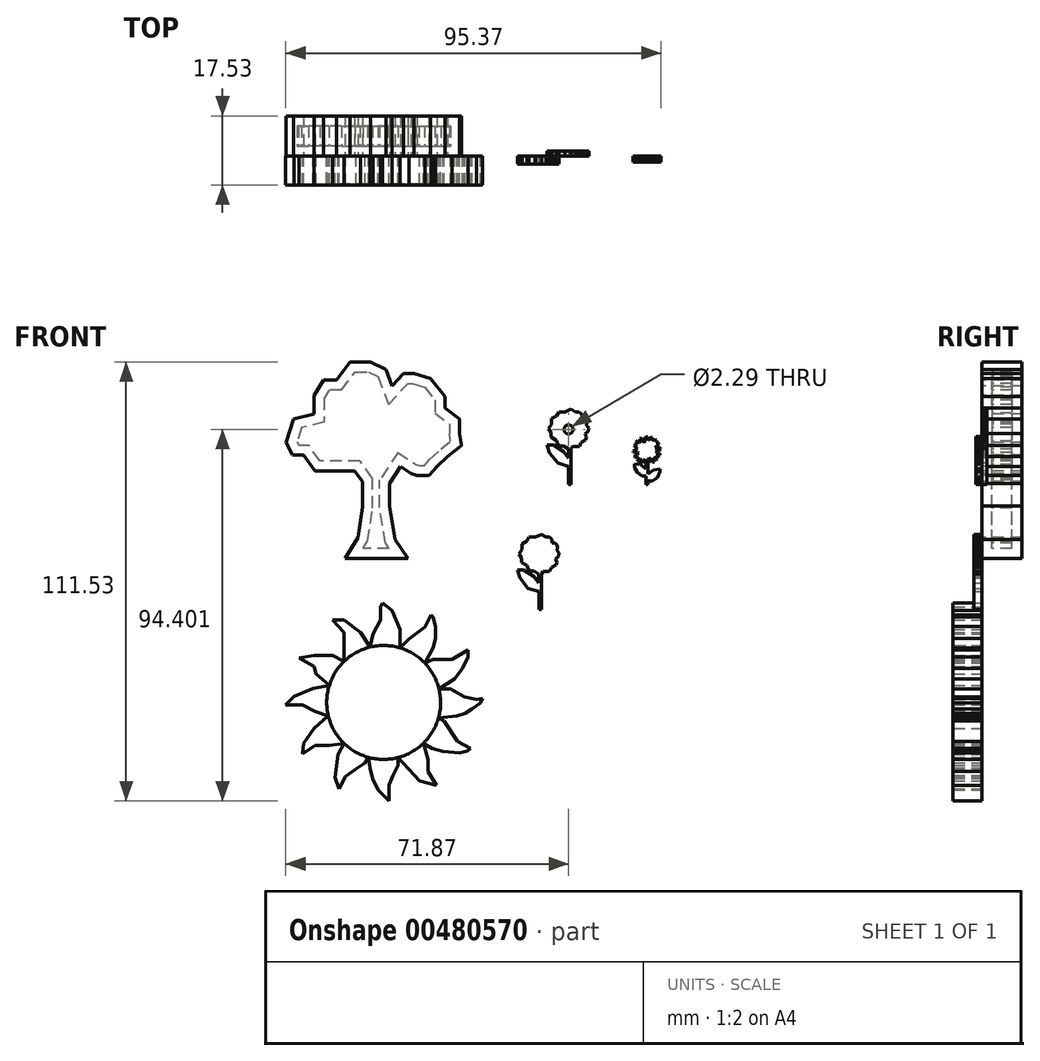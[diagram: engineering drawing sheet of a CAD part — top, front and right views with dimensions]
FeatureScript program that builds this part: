
annotation { "Feature Type Name" : "Feature", "Feature Type Description" : "" }
export const myFeature = defineFeature(function(context is Context, id is Id, definition is map)
    precondition{}
    {
        {
            var Q0;
            Q0=qCreatedBy(makeId("Front.planeOp"),FACE);
            var sketch = newSketch(context, id + "F0", { "sketchPlane" : qUnion([Q0])});
            skLineSegment(sketch, "E0", {"start": v(-33.39, 1.15) * mm, "end": v(-36.7, 6.04) * mm});
            skLineSegment(sketch, "E1", {"start": v(-36.7, 6.04) * mm, "end": v(-38.13, 14.53) * mm});
            skLineSegment(sketch, "E2", {"start": v(-38.13, 14.53) * mm, "end": v(-38.13, 20.3) * mm});
            skLineSegment(sketch, "E3", {"start": v(-49.36, 1.15) * mm, "end": v(-46.05, 6.48) * mm});
            skLineSegment(sketch, "E4", {"start": v(-46.05, 6.48) * mm, "end": v(-44.9, 14.25) * mm});
            skLineSegment(sketch, "E5", {"start": v(-44.9, 14.25) * mm, "end": v(-44.9, 20.72) * mm});
            skLineSegment(sketch, "E6", {"start": v(-44.9, 20.72) * mm, "end": v(-46.91, 23.46) * mm});
            skLineSegment(sketch, "E7", {"start": v(-28.06, 22.24) * mm, "end": v(-26.05, 24.6) * mm});
            skLineSegment(sketch, "E8", {"start": v(-46.91, 23.46) * mm, "end": v(-49.8, 23.46) * mm});
            skLineSegment(sketch, "E9", {"start": v(-49.8, 23.46) * mm, "end": v(-52.81, 23.46) * mm});
            skLineSegment(sketch, "E10", {"start": v(-52.81, 23.46) * mm, "end": v(-56.99, 23.46) * mm});
            skLineSegment(sketch, "E11", {"start": v(-56.99, 23.46) * mm, "end": v(-58.52, 25.54) * mm});
            skLineSegment(sketch, "E12", {"start": v(-58.52, 25.54) * mm, "end": v(-59.94, 27.46) * mm});
            skLineSegment(sketch, "E13", {"start": v(-51.52, 46.48) * mm, "end": v(-54.83, 46.48) * mm});
            skLineSegment(sketch, "E14", {"start": v(-54.83, 46.48) * mm, "end": v(-57.27, 42.6) * mm});
            skLineSegment(sketch, "E15", {"start": v(-57.27, 42.6) * mm, "end": v(-57.27, 37.85) * mm});
            skLineSegment(sketch, "E16", {"start": v(-57.27, 37.85) * mm, "end": v(-62.45, 36.55) * mm});
            skLineSegment(sketch, "E17", {"start": v(-62.45, 36.55) * mm, "end": v(-64.32, 30.65) * mm});
            skLineSegment(sketch, "E18", {"start": v(-64.32, 30.65) * mm, "end": v(-62.74, 27.46) * mm});
            skLineSegment(sketch, "E19", {"start": v(-62.74, 27.46) * mm, "end": v(-59.94, 27.46) * mm});
            skLineSegment(sketch, "E20", {"start": v(-51.52, 46.48) * mm, "end": v(-48.06, 51.09) * mm});
            skLineSegment(sketch, "E21", {"start": v(-48.06, 51.09) * mm, "end": v(-42.88, 51.09) * mm});
            skLineSegment(sketch, "E22", {"start": v(-42.88, 51.09) * mm, "end": v(-39, 49.21) * mm});
            skLineSegment(sketch, "E23", {"start": v(-39, 49.21) * mm, "end": v(-37.41, 45.04) * mm});
            skLineSegment(sketch, "E24", {"start": v(-37.41, 45.04) * mm, "end": v(-34.54, 48.2) * mm});
            skLineSegment(sketch, "E25", {"start": v(-34.54, 48.2) * mm, "end": v(-31.8, 48.2) * mm});
            skLineSegment(sketch, "E26", {"start": v(-31.8, 48.2) * mm, "end": v(-27.63, 46.91) * mm});
            skLineSegment(sketch, "E27", {"start": v(-27.63, 46.91) * mm, "end": v(-24.03, 42.3) * mm});
            skLineSegment(sketch, "E28", {"start": v(-24.03, 42.3) * mm, "end": v(-24.03, 39.43) * mm});
            skLineSegment(sketch, "E29", {"start": v(-24.03, 39.43) * mm, "end": v(-20.3, 36.55) * mm});
            skLineSegment(sketch, "E30", {"start": v(-20.3, 36.55) * mm, "end": v(-20.3, 32.95) * mm});
            skLineSegment(sketch, "E31", {"start": v(-26.05, 24.6) * mm, "end": v(-23.31, 27.05) * mm});
            skLineSegment(sketch, "E32", {"start": v(-23.31, 27.05) * mm, "end": v(-19.86, 29.93) * mm});
            skLineSegment(sketch, "E33", {"start": v(-19.86, 29.93) * mm, "end": v(-20.3, 32.95) * mm});
            skLineSegment(sketch, "E34", {"start": v(-35.26, 24.6) * mm, "end": v(-38.13, 20.3) * mm});
            skLineSegment(sketch, "E35", {"start": v(-35.26, 24.6) * mm, "end": v(-32.57, 22.81) * mm});
            skLineSegment(sketch, "E36", {"start": v(-32.57, 22.81) * mm, "end": v(-31.1, 22.24) * mm});
            skLineSegment(sketch, "E37", {"start": v(-31.1, 22.24) * mm, "end": v(-28.06, 22.24) * mm});
            skLineSegment(sketch, "E38", {"start": v(-33.39, 1.15) * mm, "end": v(-49.36, 1.15) * mm});
            skSolve(sketch);
        }
        {
            var Q0;
            Q0=makeQuery(id+"F0.imprint","IMPRINT",FACE,{"disambiguationData":[TD([[makeQuery(id+"F0.imprint","IMPRINT",EDGE,{"derivedFrom":sQuery(id+"F0.wireOp",EDGE,"E0")}),1.0]])]});
            extrude(context, id + "F1", {"entities" : qUnion([Q0]), "oppositeDirection" : true, "depth" : 10.16 * mm});
        }
        {
            var Q0;
            Q0=makeQuery(id+"F1.opExtrude","CAP_FACE",FACE,{"disambiguationData":[OSD([sQuery(id+"F0.wireOp",EDGE,"E0"),sQuery(id+"F0.wireOp",EDGE,"E1"),sQuery(id+"F0.wireOp",EDGE,"E2"),sQuery(id+"F0.wireOp",EDGE,"E3"),sQuery(id+"F0.wireOp",EDGE,"E4"),sQuery(id+"F0.wireOp",EDGE,"E5"),sQuery(id+"F0.wireOp",EDGE,"E6"),sQuery(id+"F0.wireOp",EDGE,"E7"),sQuery(id+"F0.wireOp",EDGE,"E8"),sQuery(id+"F0.wireOp",EDGE,"E9"),sQuery(id+"F0.wireOp",EDGE,"E10"),sQuery(id+"F0.wireOp",EDGE,"E11"),sQuery(id+"F0.wireOp",EDGE,"E12"),sQuery(id+"F0.wireOp",EDGE,"E13"),sQuery(id+"F0.wireOp",EDGE,"E14"),sQuery(id+"F0.wireOp",EDGE,"E15"),sQuery(id+"F0.wireOp",EDGE,"E16"),sQuery(id+"F0.wireOp",EDGE,"E17"),sQuery(id+"F0.wireOp",EDGE,"E18"),sQuery(id+"F0.wireOp",EDGE,"E19"),sQuery(id+"F0.wireOp",EDGE,"E20"),sQuery(id+"F0.wireOp",EDGE,"E21"),sQuery(id+"F0.wireOp",EDGE,"E22"),sQuery(id+"F0.wireOp",EDGE,"E23"),sQuery(id+"F0.wireOp",EDGE,"E24"),sQuery(id+"F0.wireOp",EDGE,"E25"),sQuery(id+"F0.wireOp",EDGE,"E26"),sQuery(id+"F0.wireOp",EDGE,"E27"),sQuery(id+"F0.wireOp",EDGE,"E28"),sQuery(id+"F0.wireOp",EDGE,"E29"),sQuery(id+"F0.wireOp",EDGE,"E30"),sQuery(id+"F0.wireOp",EDGE,"E31"),sQuery(id+"F0.wireOp",EDGE,"E32"),sQuery(id+"F0.wireOp",EDGE,"E33"),sQuery(id+"F0.wireOp",EDGE,"E34"),sQuery(id+"F0.wireOp",EDGE,"E35"),sQuery(id+"F0.wireOp",EDGE,"E36"),sQuery(id+"F0.wireOp",EDGE,"E37"),sQuery(id+"F0.wireOp",EDGE,"E38")])],"isStart":true});
            var Q1;
            Q1=makeQuery(id+"F1.opExtrude","SWEPT_BODY",BODY,{"disambiguationData":[OSD([sQuery(id+"F0.wireOp",EDGE,"E0"),sQuery(id+"F0.wireOp",EDGE,"E1"),sQuery(id+"F0.wireOp",EDGE,"E2"),sQuery(id+"F0.wireOp",EDGE,"E3"),sQuery(id+"F0.wireOp",EDGE,"E4"),sQuery(id+"F0.wireOp",EDGE,"E5"),sQuery(id+"F0.wireOp",EDGE,"E6"),sQuery(id+"F0.wireOp",EDGE,"E7"),sQuery(id+"F0.wireOp",EDGE,"E8"),sQuery(id+"F0.wireOp",EDGE,"E9"),sQuery(id+"F0.wireOp",EDGE,"E10"),sQuery(id+"F0.wireOp",EDGE,"E11"),sQuery(id+"F0.wireOp",EDGE,"E12"),sQuery(id+"F0.wireOp",EDGE,"E13"),sQuery(id+"F0.wireOp",EDGE,"E14"),sQuery(id+"F0.wireOp",EDGE,"E15"),sQuery(id+"F0.wireOp",EDGE,"E16"),sQuery(id+"F0.wireOp",EDGE,"E17"),sQuery(id+"F0.wireOp",EDGE,"E18"),sQuery(id+"F0.wireOp",EDGE,"E19"),sQuery(id+"F0.wireOp",EDGE,"E20"),sQuery(id+"F0.wireOp",EDGE,"E21"),sQuery(id+"F0.wireOp",EDGE,"E22"),sQuery(id+"F0.wireOp",EDGE,"E23"),sQuery(id+"F0.wireOp",EDGE,"E24"),sQuery(id+"F0.wireOp",EDGE,"E25"),sQuery(id+"F0.wireOp",EDGE,"E26"),sQuery(id+"F0.wireOp",EDGE,"E27"),sQuery(id+"F0.wireOp",EDGE,"E28"),sQuery(id+"F0.wireOp",EDGE,"E29"),sQuery(id+"F0.wireOp",EDGE,"E30"),sQuery(id+"F0.wireOp",EDGE,"E31"),sQuery(id+"F0.wireOp",EDGE,"E32"),sQuery(id+"F0.wireOp",EDGE,"E33"),sQuery(id+"F0.wireOp",EDGE,"E34"),sQuery(id+"F0.wireOp",EDGE,"E35"),sQuery(id+"F0.wireOp",EDGE,"E36"),sQuery(id+"F0.wireOp",EDGE,"E37"),sQuery(id+"F0.wireOp",EDGE,"E38")])]});
            shell(context, id + "F2", {"isHollow" : true, "entities" : qUnion([Q0]), "parts" : qUnion([Q1]), "thickness" : 2.54 * mm});
        }
        {
            var Q0;
            Q0=qCreatedBy(makeId("Front.planeOp"),FACE);
            var sketch = newSketch(context, id + "F3", { "sketchPlane" : qUnion([Q0])});
            skLineSegment(sketch, "E39", {"start": v(7.99, 20) * mm, "end": v(7.99, 29.07) * mm});
            skLineSegment(sketch, "E40", {"start": v(7.44, 20) * mm, "end": v(7.44, 24.53) * mm});
            skPoint(sketch, "E40.endSnap0", {"position": v(7.99, 24.53) * mm});
            skLineSegment(sketch, "E41", {"start": v(7.44, 24.53) * mm, "end": v(4.66, 25.38) * mm});
            skLineSegment(sketch, "E42", {"start": v(4.66, 25.38) * mm, "end": v(2.54, 27.98) * mm});
            skLineSegment(sketch, "E43", {"start": v(2.54, 27.98) * mm, "end": v(1.87, 30.04) * mm});
            skLineSegment(sketch, "E44", {"start": v(1.87, 30.04) * mm, "end": v(3.5, 30.04) * mm});
            skLineSegment(sketch, "E45", {"start": v(3.5, 30.04) * mm, "end": v(6.17, 28.4) * mm});
            skLineSegment(sketch, "E46", {"start": v(6.17, 28.4) * mm, "end": v(7.32, 26.77) * mm});
            skLineSegment(sketch, "E47", {"start": v(7.32, 26.77) * mm, "end": v(7.32, 29) * mm});
            skLineSegment(sketch, "E48", {"start": v(7.32, 29) * mm, "end": v(6.1, 29.73) * mm});
            skLineSegment(sketch, "E49", {"start": v(6.1, 29.73) * mm, "end": v(4.84, 29.73) * mm});
            skPoint(sketch, "E49.endSnap0", {"position": v(4.84, 29.22) * mm});
            skLineSegment(sketch, "E50", {"start": v(4.84, 29.73) * mm, "end": v(4.3, 31.13) * mm});
            skLineSegment(sketch, "E51", {"start": v(4.3, 31.13) * mm, "end": v(2.89, 31.99) * mm});
            skLineSegment(sketch, "E52", {"start": v(2.89, 31.99) * mm, "end": v(2.89, 33.12) * mm});
            skLineSegment(sketch, "E53", {"start": v(2.89, 33.12) * mm, "end": v(2.36, 34.15) * mm});
            skLineSegment(sketch, "E54", {"start": v(2.36, 34.15) * mm, "end": v(3.04, 35.27) * mm});
            skLineSegment(sketch, "E55", {"start": v(3.04, 35.27) * mm, "end": v(3.04, 36.7) * mm});
            skLineSegment(sketch, "E56", {"start": v(3.04, 36.7) * mm, "end": v(4.3, 37.36) * mm});
            skLineSegment(sketch, "E57", {"start": v(4.3, 37.36) * mm, "end": v(4.91, 38.37) * mm});
            skLineSegment(sketch, "E58", {"start": v(4.91, 38.37) * mm, "end": v(6.53, 38.37) * mm});
            skLineSegment(sketch, "E59", {"start": v(6.53, 38.37) * mm, "end": v(7.99, 39.11) * mm});
            skLineSegment(sketch, "E60", {"start": v(7.99, 39.11) * mm, "end": v(9.2, 38.37) * mm});
            skLineSegment(sketch, "E61", {"start": v(7.99, 29.07) * mm, "end": v(8.42, 29.67) * mm});
            skLineSegment(sketch, "E62", {"start": v(8.42, 29.67) * mm, "end": v(10.12, 29.67) * mm});
            skLineSegment(sketch, "E63", {"start": v(10.12, 29.67) * mm, "end": v(10.52, 30.7) * mm});
            skLineSegment(sketch, "E64", {"start": v(10.52, 30.7) * mm, "end": v(11.7, 31.3) * mm});
            skLineSegment(sketch, "E65", {"start": v(11.7, 31.3) * mm, "end": v(11.95, 32) * mm});
            skLineSegment(sketch, "E66", {"start": v(11.95, 32) * mm, "end": v(11.59, 32.81) * mm});
            skLineSegment(sketch, "E67", {"start": v(11.59, 32.81) * mm, "end": v(12.36, 33.43) * mm});
            skLineSegment(sketch, "E68", {"start": v(12.36, 33.43) * mm, "end": v(12.53, 34.35) * mm});
            skLineSegment(sketch, "E69", {"start": v(12.53, 34.35) * mm, "end": v(11.95, 34.95) * mm});
            skLineSegment(sketch, "E70", {"start": v(11.95, 34.95) * mm, "end": v(12.1, 35.77) * mm});
            skLineSegment(sketch, "E71", {"start": v(12.1, 35.77) * mm, "end": v(11.95, 36.38) * mm});
            skLineSegment(sketch, "E72", {"start": v(11.95, 36.38) * mm, "end": v(11.5, 36.84) * mm});
            skLineSegment(sketch, "E73", {"start": v(11.5, 36.84) * mm, "end": v(10.76, 36.84) * mm});
            skLineSegment(sketch, "E74", {"start": v(10.76, 36.84) * mm, "end": v(10.76, 37.73) * mm});
            skLineSegment(sketch, "E75", {"start": v(10.76, 37.73) * mm, "end": v(10.1, 38.4) * mm});
            skLineSegment(sketch, "E76", {"start": v(10.1, 38.4) * mm, "end": v(9.2, 38.37) * mm});
            skLineSegment(sketch, "E77", {"start": v(7.99, 20) * mm, "end": v(7.44, 20) * mm});
            skLineSegment(sketch, "E78", {"start": v(7.32, 26.77) * mm, "end": v(7.44, 24.53) * mm});
            skSolve(sketch);
        }
        {
            var Q0;
            Q0=makeQuery(id+"F3.imprint","IMPRINT",FACE,{"disambiguationData":[TD([[makeQuery(id+"F3.imprint","IMPRINT",EDGE,{"derivedFrom":sQuery(id+"F3.wireOp",EDGE,"E39")}),1.0]])]});
            var Q1;
            Q1=makeQuery(id+"F3.imprint","IMPRINT",FACE,{"disambiguationData":[TD([[makeQuery(id+"F3.imprint","IMPRINT",EDGE,{"derivedFrom":sQuery(id+"F3.wireOp",EDGE,"E41")}),-1.0]])]});
            extrude(context, id + "F4", {"entities" : qUnion([Q0, Q1]), "oppositeDirection" : true, "depth" : 1.27 * mm});
        }
        {
            var Q0;
            Q0=qCreatedBy(makeId("Front.planeOp"),FACE);
            var sketch = newSketch(context, id + "F5", { "sketchPlane" : qUnion([Q0])});
            skCircle(sketch, "E79", {"center": v(7.4, 33.96) * mm, "radius": 1.58 * mm});
            skSolve(sketch);
        }
        {
            var Q0;
            Q0=sQuery(id+"F5.wireOp",VERTEX,"E79.center");
            var Q1;
            Q1=makeQuery(id+"F4.opExtrude","SWEPT_BODY",BODY,{"disambiguationData":[OSD([sQuery(id+"F3.wireOp",EDGE,"E39"),sQuery(id+"F3.wireOp",EDGE,"E40"),sQuery(id+"F3.wireOp",EDGE,"E41"),sQuery(id+"F3.wireOp",EDGE,"E42"),sQuery(id+"F3.wireOp",EDGE,"E43"),sQuery(id+"F3.wireOp",EDGE,"E44"),sQuery(id+"F3.wireOp",EDGE,"E45"),sQuery(id+"F3.wireOp",EDGE,"E46"),sQuery(id+"F3.wireOp",EDGE,"E47"),sQuery(id+"F3.wireOp",EDGE,"E48"),sQuery(id+"F3.wireOp",EDGE,"E49"),sQuery(id+"F3.wireOp",EDGE,"E50"),sQuery(id+"F3.wireOp",EDGE,"E51"),sQuery(id+"F3.wireOp",EDGE,"E52"),sQuery(id+"F3.wireOp",EDGE,"E53"),sQuery(id+"F3.wireOp",EDGE,"E54"),sQuery(id+"F3.wireOp",EDGE,"E55"),sQuery(id+"F3.wireOp",EDGE,"E56"),sQuery(id+"F3.wireOp",EDGE,"E57"),sQuery(id+"F3.wireOp",EDGE,"E58"),sQuery(id+"F3.wireOp",EDGE,"E59"),sQuery(id+"F3.wireOp",EDGE,"E60"),sQuery(id+"F3.wireOp",EDGE,"E61"),sQuery(id+"F3.wireOp",EDGE,"E62"),sQuery(id+"F3.wireOp",EDGE,"E63"),sQuery(id+"F3.wireOp",EDGE,"E64"),sQuery(id+"F3.wireOp",EDGE,"E65"),sQuery(id+"F3.wireOp",EDGE,"E66"),sQuery(id+"F3.wireOp",EDGE,"E67"),sQuery(id+"F3.wireOp",EDGE,"E68"),sQuery(id+"F3.wireOp",EDGE,"E69"),sQuery(id+"F3.wireOp",EDGE,"E70"),sQuery(id+"F3.wireOp",EDGE,"E71"),sQuery(id+"F3.wireOp",EDGE,"E72"),sQuery(id+"F3.wireOp",EDGE,"E73"),sQuery(id+"F3.wireOp",EDGE,"E74"),sQuery(id+"F3.wireOp",EDGE,"E75"),sQuery(id+"F3.wireOp",EDGE,"E76"),sQuery(id+"F3.wireOp",EDGE,"E77")])]});
            hole(context, id + "F6", {"style" : HoleStyle.C_BORE, "endStyle" : HoleEndStyle.THROUGH, "holeDiameter" : 1.14 * mm, "cBoreDiameter" : 2.3 * mm, "cBoreDepth" : 12.7 * mm, "tappedDepth" : 12.7 * mm, "tapClearance" : 3, "locations" : qUnion([Q0]), "scope" : qUnion([Q1])});
        }
        {
            var Q0;
            Q0=qCreatedBy(makeId("Front.planeOp"),FACE);
            var sketch = newSketch(context, id + "F7", { "sketchPlane" : qUnion([Q0])});
            skLineSegment(sketch, "E80", {"start": v(0.48, -11.79) * mm, "end": v(0.48, -2.71) * mm});
            skLineSegment(sketch, "E81", {"start": v(-0.06, -11.79) * mm, "end": v(-0.06, -7.25) * mm});
            skPoint(sketch, "E81.endSnap0", {"position": v(0.48, -7.25) * mm});
            skLineSegment(sketch, "E82", {"start": v(-0.06, -7.25) * mm, "end": v(-2.85, -6.4) * mm});
            skLineSegment(sketch, "E83", {"start": v(-2.85, -6.4) * mm, "end": v(-4.96, -3.8) * mm});
            skLineSegment(sketch, "E84", {"start": v(-4.96, -3.8) * mm, "end": v(-5.63, -1.74) * mm});
            skLineSegment(sketch, "E85", {"start": v(-5.63, -1.74) * mm, "end": v(-4, -1.74) * mm});
            skLineSegment(sketch, "E86", {"start": v(-4, -1.74) * mm, "end": v(-1.33, -3.38) * mm});
            skLineSegment(sketch, "E87", {"start": v(-1.33, -3.38) * mm, "end": v(-0.18, -5.01) * mm});
            skLineSegment(sketch, "E88", {"start": v(-0.18, -5.01) * mm, "end": v(-0.18, -2.77) * mm});
            skLineSegment(sketch, "E89", {"start": v(-0.18, -2.77) * mm, "end": v(-1.4, -2.05) * mm});
            skLineSegment(sketch, "E90", {"start": v(-1.4, -2.05) * mm, "end": v(-2.66, -2.05) * mm});
            skPoint(sketch, "E90.endSnap0", {"position": v(-2.66, -2.56) * mm});
            skLineSegment(sketch, "E91", {"start": v(-2.66, -2.05) * mm, "end": v(-3.2, -0.66) * mm});
            skLineSegment(sketch, "E92", {"start": v(-3.2, -0.66) * mm, "end": v(-4.61, 0.2) * mm});
            skLineSegment(sketch, "E93", {"start": v(-4.61, 0.2) * mm, "end": v(-4.61, 1.34) * mm});
            skLineSegment(sketch, "E94", {"start": v(-4.61, 1.34) * mm, "end": v(-5.15, 2.37) * mm});
            skLineSegment(sketch, "E95", {"start": v(-5.15, 2.37) * mm, "end": v(-4.46, 3.49) * mm});
            skLineSegment(sketch, "E96", {"start": v(-4.46, 3.49) * mm, "end": v(-4.46, 4.91) * mm});
            skLineSegment(sketch, "E97", {"start": v(-4.46, 4.91) * mm, "end": v(-3.2, 5.58) * mm});
            skLineSegment(sketch, "E98", {"start": v(-3.2, 5.58) * mm, "end": v(-2.59, 6.59) * mm});
            skLineSegment(sketch, "E99", {"start": v(-2.59, 6.59) * mm, "end": v(-0.97, 6.59) * mm});
            skLineSegment(sketch, "E100", {"start": v(-0.97, 6.59) * mm, "end": v(0.48, 7.33) * mm});
            skLineSegment(sketch, "E101", {"start": v(0.48, 7.33) * mm, "end": v(1.7, 6.59) * mm});
            skLineSegment(sketch, "E102", {"start": v(0.48, -2.71) * mm, "end": v(0.92, -2.11) * mm});
            skLineSegment(sketch, "E103", {"start": v(0.92, -2.11) * mm, "end": v(2.62, -2.11) * mm});
            skLineSegment(sketch, "E104", {"start": v(2.62, -2.11) * mm, "end": v(3.01, -1.09) * mm});
            skLineSegment(sketch, "E105", {"start": v(3.01, -1.09) * mm, "end": v(4.2, -0.49) * mm});
            skLineSegment(sketch, "E106", {"start": v(4.2, -0.49) * mm, "end": v(4.45, 0.22) * mm});
            skLineSegment(sketch, "E107", {"start": v(4.45, 0.22) * mm, "end": v(4.08, 1.03) * mm});
            skLineSegment(sketch, "E108", {"start": v(4.08, 1.03) * mm, "end": v(4.85, 1.65) * mm});
            skLineSegment(sketch, "E109", {"start": v(4.85, 1.65) * mm, "end": v(5.02, 2.57) * mm});
            skLineSegment(sketch, "E110", {"start": v(5.02, 2.57) * mm, "end": v(4.45, 3.17) * mm});
            skLineSegment(sketch, "E111", {"start": v(4.45, 3.17) * mm, "end": v(4.6, 4) * mm});
            skLineSegment(sketch, "E112", {"start": v(4.6, 4) * mm, "end": v(4.45, 4.6) * mm});
            skLineSegment(sketch, "E113", {"start": v(4.45, 4.6) * mm, "end": v(4, 5.06) * mm});
            skLineSegment(sketch, "E114", {"start": v(4, 5.06) * mm, "end": v(3.25, 5.06) * mm});
            skLineSegment(sketch, "E115", {"start": v(3.25, 5.06) * mm, "end": v(3.25, 5.95) * mm});
            skLineSegment(sketch, "E116", {"start": v(3.25, 5.95) * mm, "end": v(2.6, 6.62) * mm});
            skLineSegment(sketch, "E117", {"start": v(2.6, 6.62) * mm, "end": v(1.7, 6.59) * mm});
            skLineSegment(sketch, "E118", {"start": v(0.48, -11.79) * mm, "end": v(-0.06, -11.79) * mm});
            skLineSegment(sketch, "E119", {"start": v(-0.18, -5.01) * mm, "end": v(-0.06, -7.25) * mm});
            skSolve(sketch);
        }
        {
            var Q0;
            Q0=makeQuery(id+"F7.imprint","IMPRINT",FACE,{"disambiguationData":[TD([[makeQuery(id+"F7.imprint","IMPRINT",EDGE,{"derivedFrom":sQuery(id+"F7.wireOp",EDGE,"E80")}),1.0]])]});
            var Q1;
            Q1=makeQuery(id+"F7.imprint","IMPRINT",FACE,{"disambiguationData":[TD([[makeQuery(id+"F7.imprint","IMPRINT",EDGE,{"derivedFrom":sQuery(id+"F7.wireOp",EDGE,"E82")}),-1.0]])]});
            extrude(context, id + "F8", {"entities" : qUnion([Q0, Q1]), "depth" : 2.03 * mm});
        }
        {
            var Q0;
            Q0=qCreatedBy(makeId("Front.planeOp"),FACE);
            var sketch = newSketch(context, id + "F9", { "sketchPlane" : qUnion([Q0])});
            skLineSegment(sketch, "E120", {"start": v(27.09, 20.02) * mm, "end": v(27.09, 22.14) * mm});
            skLineSegment(sketch, "E121", {"start": v(27.09, 22.14) * mm, "end": v(26.1, 22.14) * mm});
            skLineSegment(sketch, "E122", {"start": v(26.1, 22.14) * mm, "end": v(24.9, 23.02) * mm});
            skLineSegment(sketch, "E123", {"start": v(24.9, 23.02) * mm, "end": v(24.14, 24.3) * mm});
            skLineSegment(sketch, "E124", {"start": v(24.14, 24.3) * mm, "end": v(24.14, 25.24) * mm});
            skLineSegment(sketch, "E125", {"start": v(24.14, 25.24) * mm, "end": v(25.27, 25.06) * mm});
            skLineSegment(sketch, "E126", {"start": v(25.27, 25.06) * mm, "end": v(25.27, 25.89) * mm});
            skLineSegment(sketch, "E127", {"start": v(28.72, 20.83) * mm, "end": v(29.97, 21.8) * mm});
            skLineSegment(sketch, "E128", {"start": v(29.97, 21.8) * mm, "end": v(30.6, 23.25) * mm});
            skLineSegment(sketch, "E129", {"start": v(30.6, 23.25) * mm, "end": v(30.6, 23.93) * mm});
            skLineSegment(sketch, "E130", {"start": v(30.6, 23.93) * mm, "end": v(29, 23.65) * mm});
            skLineSegment(sketch, "E131", {"start": v(29, 23.65) * mm, "end": v(28.04, 23) * mm});
            skLineSegment(sketch, "E132", {"start": v(27.55, 25.12) * mm, "end": v(27.13, 25.7) * mm});
            skLineSegment(sketch, "E133", {"start": v(27.13, 25.7) * mm, "end": v(27.13, 23.97) * mm});
            skLineSegment(sketch, "E134", {"start": v(27.13, 23.97) * mm, "end": v(25.74, 24.96) * mm});
            skLineSegment(sketch, "E135", {"start": v(25.74, 24.96) * mm, "end": v(25.74, 26.1) * mm});
            skLineSegment(sketch, "E136", {"start": v(25.74, 26.1) * mm, "end": v(25.27, 25.89) * mm});
            skLineSegment(sketch, "E137", {"start": v(27.55, 25.12) * mm, "end": v(27.55, 22.66) * mm});
            skLineSegment(sketch, "E138", {"start": v(27.6, 20.8) * mm, "end": v(27.6, 20.02) * mm});
            skLineSegment(sketch, "E139", {"start": v(27.6, 20.02) * mm, "end": v(27.09, 20.02) * mm});
            skLineSegment(sketch, "E140", {"start": v(27.6, 20.8) * mm, "end": v(27.55, 22.66) * mm});
            skLineSegment(sketch, "E141", {"start": v(27.6, 20.8) * mm, "end": v(28.72, 20.83) * mm});
            skLineSegment(sketch, "E142", {"start": v(28.04, 23) * mm, "end": v(27.55, 22.66) * mm});
            skLineSegment(sketch, "E143", {"start": v(26.95, 26.45) * mm, "end": v(26.36, 25.46) * mm});
            skLineSegment(sketch, "E144", {"start": v(26.36, 25.46) * mm, "end": v(26.13, 25.6) * mm});
            skLineSegment(sketch, "E145", {"start": v(26.13, 25.6) * mm, "end": v(26.11, 26.3) * mm});
            skLineSegment(sketch, "E146", {"start": v(26.11, 26.3) * mm, "end": v(25.88, 26.3) * mm});
            skLineSegment(sketch, "E147", {"start": v(25.88, 26.3) * mm, "end": v(25.07, 25.95) * mm});
            skLineSegment(sketch, "E148", {"start": v(25.07, 25.95) * mm, "end": v(24.93, 26.3) * mm});
            skLineSegment(sketch, "E149", {"start": v(24.93, 26.3) * mm, "end": v(25.17, 26.92) * mm});
            skLineSegment(sketch, "E150", {"start": v(25.17, 26.92) * mm, "end": v(24.33, 26.9) * mm});
            skLineSegment(sketch, "E151", {"start": v(24.33, 26.9) * mm, "end": v(24.32, 27.42) * mm});
            skLineSegment(sketch, "E152", {"start": v(24.32, 27.42) * mm, "end": v(25.3, 28) * mm});
            skLineSegment(sketch, "E153", {"start": v(25.3, 28) * mm, "end": v(23.94, 28.23) * mm});
            skLineSegment(sketch, "E154", {"start": v(23.94, 28.23) * mm, "end": v(23.82, 28.48) * mm});
            skLineSegment(sketch, "E155", {"start": v(23.82, 28.48) * mm, "end": v(24.5, 28.8) * mm});
            skLineSegment(sketch, "E156", {"start": v(24.5, 28.8) * mm, "end": v(24.9, 29) * mm});
            skLineSegment(sketch, "E157", {"start": v(24.9, 29) * mm, "end": v(24, 29.88) * mm});
            skLineSegment(sketch, "E158", {"start": v(24, 29.88) * mm, "end": v(24.5, 30.12) * mm});
            skLineSegment(sketch, "E159", {"start": v(24.5, 30.12) * mm, "end": v(24.9, 30.13) * mm});
            skLineSegment(sketch, "E160", {"start": v(24.9, 30.13) * mm, "end": v(24.5, 30.94) * mm});
            skLineSegment(sketch, "E161", {"start": v(24.5, 30.94) * mm, "end": v(24.9, 31.13) * mm});
            skLineSegment(sketch, "E162", {"start": v(24.9, 31.13) * mm, "end": v(25.78, 30.52) * mm});
            skLineSegment(sketch, "E163", {"start": v(25.78, 30.52) * mm, "end": v(25.54, 31.61) * mm});
            skLineSegment(sketch, "E164", {"start": v(25.54, 31.61) * mm, "end": v(26.11, 31.74) * mm});
            skLineSegment(sketch, "E165", {"start": v(26.11, 31.74) * mm, "end": v(26.7, 30.52) * mm});
            skLineSegment(sketch, "E166", {"start": v(26.7, 30.52) * mm, "end": v(26.9, 32.16) * mm});
            skLineSegment(sketch, "E167", {"start": v(26.9, 32.16) * mm, "end": v(27.39, 32.1) * mm});
            skLineSegment(sketch, "E168", {"start": v(27.39, 32.1) * mm, "end": v(27.6, 31.1) * mm});
            skLineSegment(sketch, "E169", {"start": v(27.6, 31.1) * mm, "end": v(28.36, 32.06) * mm});
            skLineSegment(sketch, "E170", {"start": v(28.36, 32.06) * mm, "end": v(28.61, 31.85) * mm});
            skLineSegment(sketch, "E171", {"start": v(28.61, 31.85) * mm, "end": v(28.63, 31.1) * mm});
            skLineSegment(sketch, "E172", {"start": v(27.88, 26.81) * mm, "end": v(28.76, 25.69) * mm});
            skLineSegment(sketch, "E173", {"start": v(28.76, 25.69) * mm, "end": v(29.2, 25.69) * mm});
            skLineSegment(sketch, "E174", {"start": v(29.2, 25.69) * mm, "end": v(28.82, 26.9) * mm});
            skLineSegment(sketch, "E175", {"start": v(28.82, 26.9) * mm, "end": v(29.65, 26.3) * mm});
            skLineSegment(sketch, "E176", {"start": v(29.65, 26.3) * mm, "end": v(30.01, 26.45) * mm});
            skLineSegment(sketch, "E177", {"start": v(30.01, 26.45) * mm, "end": v(29.62, 27.33) * mm});
            skLineSegment(sketch, "E178", {"start": v(29.62, 27.33) * mm, "end": v(30.68, 27.33) * mm});
            skLineSegment(sketch, "E179", {"start": v(30.68, 27.33) * mm, "end": v(30.48, 27.92) * mm});
            skLineSegment(sketch, "E180", {"start": v(30.48, 27.92) * mm, "end": v(29.53, 28.4) * mm});
            skLineSegment(sketch, "E181", {"start": v(29.53, 28.4) * mm, "end": v(30.9, 28.93) * mm});
            skLineSegment(sketch, "E182", {"start": v(30.9, 28.93) * mm, "end": v(30.44, 29.33) * mm});
            skLineSegment(sketch, "E183", {"start": v(30.44, 29.33) * mm, "end": v(29.39, 29.33) * mm});
            skLineSegment(sketch, "E184", {"start": v(29.39, 29.33) * mm, "end": v(30.3, 30.14) * mm});
            skLineSegment(sketch, "E185", {"start": v(30.3, 30.14) * mm, "end": v(30.3, 30.63) * mm});
            skLineSegment(sketch, "E186", {"start": v(30.3, 30.63) * mm, "end": v(29.59, 30.63) * mm});
            skLineSegment(sketch, "E187", {"start": v(29.59, 30.63) * mm, "end": v(29.75, 31.33) * mm});
            skLineSegment(sketch, "E188", {"start": v(29.75, 31.33) * mm, "end": v(29.23, 31.45) * mm});
            skLineSegment(sketch, "E189", {"start": v(29.23, 31.45) * mm, "end": v(28.63, 31.1) * mm});
            skLineSegment(sketch, "E190", {"start": v(27.88, 26.81) * mm, "end": v(27.88, 25.54) * mm});
            skLineSegment(sketch, "E191", {"start": v(27.88, 25.54) * mm, "end": v(27.55, 25.12) * mm});
            skLineSegment(sketch, "E192", {"start": v(27.13, 25.7) * mm, "end": v(26.95, 26.45) * mm});
            skSolve(sketch);
        }
        {
            var Q0;
            Q0=makeQuery(id+"F9.imprint","IMPRINT",FACE,{"disambiguationData":[TD([[makeQuery(id+"F9.imprint","IMPRINT",EDGE,{"derivedFrom":sQuery(id+"F9.wireOp",EDGE,"E132")}),-1.0]])]});
            var Q1;
            Q1=makeQuery(id+"F9.imprint","IMPRINT",FACE,{"disambiguationData":[TD([[makeQuery(id+"F9.imprint","IMPRINT",EDGE,{"derivedFrom":sQuery(id+"F9.wireOp",EDGE,"E120")}),-1.0]])]});
            var Q2;
            Q2=makeQuery(id+"F9.imprint","IMPRINT",FACE,{"disambiguationData":[TD([[makeQuery(id+"F9.imprint","IMPRINT",EDGE,{"derivedFrom":sQuery(id+"F9.wireOp",EDGE,"E127")}),1.0]])]});
            extrude(context, id + "F10", {"entities" : qUnion([Q0, Q1, Q2]), "depth" : 1.52 * mm});
        }
        {
            var Q0;
            Q0=qCreatedBy(makeId("Front.planeOp"),FACE);
            var sketch = newSketch(context, id + "F11", { "sketchPlane" : qUnion([Q0])});
            skCircle(sketch, "E193", {"center": v(-39.57, -35.4) * mm, "radius": 14.47 * mm});
            skLineSegment(sketch, "E194", {"start": v(-43.02, -21.34) * mm, "end": v(-45.47, -17.56) * mm});
            skLineSegment(sketch, "E195", {"start": v(-45.47, -17.56) * mm, "end": v(-49.65, -14.4) * mm});
            skLineSegment(sketch, "E196", {"start": v(-49.65, -14.4) * mm, "end": v(-52.52, -14.4) * mm});
            skLineSegment(sketch, "E197", {"start": v(-52.52, -14.4) * mm, "end": v(-49.65, -17.56) * mm});
            skLineSegment(sketch, "E198", {"start": v(-49.65, -17.56) * mm, "end": v(-49.65, -21.87) * mm});
            skLineSegment(sketch, "E199", {"start": v(-49.65, -21.87) * mm, "end": v(-49.65, -25) * mm});
            skLineSegment(sketch, "E200", {"start": v(-49.65, -25) * mm, "end": v(-52.52, -23.46) * mm});
            skLineSegment(sketch, "E201", {"start": v(-52.52, -23.46) * mm, "end": v(-57.27, -23.46) * mm});
            skLineSegment(sketch, "E202", {"start": v(-57.27, -23.46) * mm, "end": v(-61.07, -24.03) * mm});
            skLineSegment(sketch, "E203", {"start": v(-61.07, -24.03) * mm, "end": v(-57.27, -26.2) * mm});
            skLineSegment(sketch, "E204", {"start": v(-57.27, -26.2) * mm, "end": v(-56.72, -28.13) * mm});
            skLineSegment(sketch, "E205", {"start": v(-56.72, -28.13) * mm, "end": v(-53.38, -31.08) * mm});
            skLineSegment(sketch, "E206", {"start": v(-35.4, -21.54) * mm, "end": v(-35.4, -16.84) * mm});
            skLineSegment(sketch, "E207", {"start": v(-35.4, -16.84) * mm, "end": v(-37.42, -12.09) * mm});
            skLineSegment(sketch, "E208", {"start": v(-42.3, -17.98) * mm, "end": v(-43.02, -21.34) * mm});
            skLineSegment(sketch, "E209", {"start": v(-42.3, -17.98) * mm, "end": v(-40.4, -14.5) * mm});
            skLineSegment(sketch, "E210", {"start": v(-40.4, -14.5) * mm, "end": v(-40.4, -11.1) * mm});
            skLineSegment(sketch, "E211", {"start": v(-40.4, -11.1) * mm, "end": v(-39.85, -10.07) * mm});
            skLineSegment(sketch, "E212", {"start": v(-39.85, -10.07) * mm, "end": v(-37.42, -12.09) * mm});
            skLineSegment(sketch, "E213", {"start": v(-29.1, -25.42) * mm, "end": v(-27, -21.54) * mm});
            skLineSegment(sketch, "E214", {"start": v(-35.4, -21.54) * mm, "end": v(-33.17, -19.28) * mm});
            skLineSegment(sketch, "E215", {"start": v(-33.17, -19.28) * mm, "end": v(-29.07, -16.27) * mm});
            skLineSegment(sketch, "E216", {"start": v(-29.07, -16.27) * mm, "end": v(-27.53, -13.15) * mm});
            skLineSegment(sketch, "E217", {"start": v(-27.53, -13.15) * mm, "end": v(-27.08, -13.72) * mm});
            skLineSegment(sketch, "E218", {"start": v(-27.08, -13.72) * mm, "end": v(-26.4, -16.08) * mm});
            skLineSegment(sketch, "E219", {"start": v(-26.4, -16.08) * mm, "end": v(-26.4, -19.17) * mm});
            skLineSegment(sketch, "E220", {"start": v(-26.4, -19.17) * mm, "end": v(-27, -21.54) * mm});
            skLineSegment(sketch, "E221", {"start": v(-29.1, -25.42) * mm, "end": v(-27, -24.5) * mm});
            skLineSegment(sketch, "E222", {"start": v(-27, -24.5) * mm, "end": v(-22.27, -24.5) * mm});
            skLineSegment(sketch, "E223", {"start": v(-22.27, -24.5) * mm, "end": v(-18.1, -22.1) * mm});
            skLineSegment(sketch, "E224", {"start": v(-18.1, -22.1) * mm, "end": v(-18.1, -23.8) * mm});
            skLineSegment(sketch, "E225", {"start": v(-18.1, -23.8) * mm, "end": v(-19.5, -26.76) * mm});
            skLineSegment(sketch, "E226", {"start": v(-19.5, -26.76) * mm, "end": v(-21.63, -29.43) * mm});
            skLineSegment(sketch, "E227", {"start": v(-21.63, -29.43) * mm, "end": v(-25.52, -31.96) * mm});
            skLineSegment(sketch, "E228", {"start": v(-25.52, -31.96) * mm, "end": v(-22.64, -31.96) * mm});
            skLineSegment(sketch, "E229", {"start": v(-22.64, -31.96) * mm, "end": v(-19.07, -33.98) * mm});
            skLineSegment(sketch, "E230", {"start": v(-19.07, -33.98) * mm, "end": v(-16.02, -34.7) * mm});
            skLineSegment(sketch, "E231", {"start": v(-16.02, -34.7) * mm, "end": v(-14.48, -34.36) * mm});
            skLineSegment(sketch, "E232", {"start": v(-14.48, -34.36) * mm, "end": v(-14.97, -35.49) * mm});
            skLineSegment(sketch, "E233", {"start": v(-14.97, -35.49) * mm, "end": v(-17.1, -37.02) * mm});
            skLineSegment(sketch, "E234", {"start": v(-17.1, -37.02) * mm, "end": v(-18.94, -38.22) * mm});
            skLineSegment(sketch, "E235", {"start": v(-18.94, -38.22) * mm, "end": v(-20.91, -38.83) * mm});
            skLineSegment(sketch, "E236", {"start": v(-20.91, -38.83) * mm, "end": v(-25.63, -39.27) * mm});
            skLineSegment(sketch, "E237", {"start": v(-25.63, -39.27) * mm, "end": v(-24.18, -40.07) * mm});
            skLineSegment(sketch, "E238", {"start": v(-24.18, -40.07) * mm, "end": v(-22.35, -42.89) * mm});
            skLineSegment(sketch, "E239", {"start": v(-22.35, -42.89) * mm, "end": v(-20.77, -45.32) * mm});
            skLineSegment(sketch, "E240", {"start": v(-20.77, -45.32) * mm, "end": v(-17.45, -47.14) * mm});
            skLineSegment(sketch, "E241", {"start": v(-17.45, -47.14) * mm, "end": v(-18.3, -47.69) * mm});
            skLineSegment(sketch, "E242", {"start": v(-18.3, -47.69) * mm, "end": v(-20.27, -48.23) * mm});
            skLineSegment(sketch, "E243", {"start": v(-20.27, -48.23) * mm, "end": v(-24.45, -47.78) * mm});
            skLineSegment(sketch, "E244", {"start": v(-24.45, -47.78) * mm, "end": v(-27.27, -47.14) * mm});
            skLineSegment(sketch, "E245", {"start": v(-27.27, -47.14) * mm, "end": v(-29.47, -45.76) * mm});
            skLineSegment(sketch, "E246", {"start": v(-29.47, -45.76) * mm, "end": v(-28.37, -49.92) * mm});
            skPoint(sketch, "E246.endSnap0", {"position": v(-28.37, -46.45) * mm});
            skLineSegment(sketch, "E247", {"start": v(-28.37, -49.92) * mm, "end": v(-28.37, -52.9) * mm});
            skLineSegment(sketch, "E248", {"start": v(-28.37, -52.9) * mm, "end": v(-26.14, -56.5) * mm});
            skLineSegment(sketch, "E249", {"start": v(-26.14, -56.5) * mm, "end": v(-30.5, -55.3) * mm});
            skLineSegment(sketch, "E250", {"start": v(-30.5, -55.3) * mm, "end": v(-35.92, -49.4) * mm});
            skLineSegment(sketch, "E251", {"start": v(-35.92, -49.4) * mm, "end": v(-35.92, -51.35) * mm});
            skLineSegment(sketch, "E252", {"start": v(-35.92, -51.35) * mm, "end": v(-37.23, -53.98) * mm});
            skLineSegment(sketch, "E253", {"start": v(-37.23, -53.98) * mm, "end": v(-38.24, -56.35) * mm});
            skLineSegment(sketch, "E254", {"start": v(-38.24, -56.35) * mm, "end": v(-38.24, -60.44) * mm});
            skLineSegment(sketch, "E255", {"start": v(-38.24, -60.44) * mm, "end": v(-40.99, -57.63) * mm});
            skLineSegment(sketch, "E256", {"start": v(-40.99, -57.63) * mm, "end": v(-42.42, -54.74) * mm});
            skLineSegment(sketch, "E257", {"start": v(-42.42, -54.74) * mm, "end": v(-43.02, -52.03) * mm});
            skLineSegment(sketch, "E258", {"start": v(-43.02, -52.03) * mm, "end": v(-43.44, -49.35) * mm});
            skLineSegment(sketch, "E259", {"start": v(-43.44, -49.35) * mm, "end": v(-44.3, -50.72) * mm});
            skLineSegment(sketch, "E260", {"start": v(-44.3, -50.72) * mm, "end": v(-46.63, -52.3) * mm});
            skLineSegment(sketch, "E261", {"start": v(-46.63, -52.3) * mm, "end": v(-49.3, -54.2) * mm});
            skLineSegment(sketch, "E262", {"start": v(-49.3, -54.2) * mm, "end": v(-50.92, -57.37) * mm});
            skLineSegment(sketch, "E263", {"start": v(-50.92, -57.37) * mm, "end": v(-51.97, -54.4) * mm});
            skLineSegment(sketch, "E264", {"start": v(-51.97, -54.4) * mm, "end": v(-51.14, -48.57) * mm});
            skLineSegment(sketch, "E265", {"start": v(-51.14, -48.57) * mm, "end": v(-49.68, -45.76) * mm});
            skLineSegment(sketch, "E266", {"start": v(-49.68, -45.76) * mm, "end": v(-53.36, -46.35) * mm});
            skLineSegment(sketch, "E267", {"start": v(-53.36, -46.35) * mm, "end": v(-57.04, -46.35) * mm});
            skLineSegment(sketch, "E268", {"start": v(-57.04, -46.35) * mm, "end": v(-60.24, -48.53) * mm});
            skLineSegment(sketch, "E269", {"start": v(-60.24, -48.53) * mm, "end": v(-59.9, -45.76) * mm});
            skLineSegment(sketch, "E270", {"start": v(-59.9, -45.76) * mm, "end": v(-57.23, -42) * mm});
            skLineSegment(sketch, "E271", {"start": v(-57.23, -42) * mm, "end": v(-53.65, -38.77) * mm});
            skLineSegment(sketch, "E272", {"start": v(-53.65, -38.77) * mm, "end": v(-57.04, -37.7) * mm});
            skLineSegment(sketch, "E273", {"start": v(-57.04, -37.7) * mm, "end": v(-60.16, -36.08) * mm});
            skLineSegment(sketch, "E274", {"start": v(-60.16, -36.08) * mm, "end": v(-64.47, -36.08) * mm});
            skLineSegment(sketch, "E275", {"start": v(-64.47, -36.08) * mm, "end": v(-62.3, -33.9) * mm});
            skLineSegment(sketch, "E276", {"start": v(-62.3, -33.9) * mm, "end": v(-57.53, -31.8) * mm});
            skLineSegment(sketch, "E277", {"start": v(-57.53, -31.8) * mm, "end": v(-53.38, -31.08) * mm});
            skSolve(sketch);
        }
        {
            var Q0;
            {var subQ0=sQuery(id+"F11.wireOp",EDGE,"E259");Q0=makeQuery(id+"F11.imprint","IMPRINT",FACE,{"disambiguationData":[TD([[makeQuery(id+"F11.imprint","IMPRINT",EDGE,{"derivedFrom":subQ0}),-1.0]])]});}
            var Q1;
            {var subQ0=sQuery(id+"F11.wireOp",EDGE,"E266");Q1=makeQuery(id+"F11.imprint","IMPRINT",FACE,{"disambiguationData":[TD([[makeQuery(id+"F11.imprint","IMPRINT",EDGE,{"derivedFrom":subQ0}),-1.0]])]});}
            var Q2;
            {var subQ0=sQuery(id+"F11.wireOp",EDGE,"E272");Q2=makeQuery(id+"F11.imprint","IMPRINT",FACE,{"disambiguationData":[TD([[makeQuery(id+"F11.imprint","IMPRINT",EDGE,{"derivedFrom":subQ0}),-1.0]])]});}
            var Q3;
            {var subQ0=sQuery(id+"F11.wireOp",EDGE,"E200");Q3=makeQuery(id+"F11.imprint","IMPRINT",FACE,{"disambiguationData":[TD([[makeQuery(id+"F11.imprint","IMPRINT",EDGE,{"derivedFrom":subQ0}),1.0]])]});}
            var Q4;
            {var subQ0=sQuery(id+"F11.wireOp",EDGE,"E194");Q4=makeQuery(id+"F11.imprint","IMPRINT",FACE,{"disambiguationData":[TD([[makeQuery(id+"F11.imprint","IMPRINT",EDGE,{"derivedFrom":subQ0}),1.0]])]});}
            var Q5;
            {var subQ1=sQuery(id+"F11.wireOp",EDGE,"E206");Q5=makeQuery(id+"F11.imprint","IMPRINT",FACE,{"disambiguationData":[TD([[makeQuery(id+"F11.imprint","IMPRINT",EDGE,{"derivedFrom":subQ1}),1.0]])]});}
            var Q6;
            {var subQ1=sQuery(id+"F11.wireOp",EDGE,"E213");Q6=makeQuery(id+"F11.imprint","IMPRINT",FACE,{"disambiguationData":[TD([[makeQuery(id+"F11.imprint","IMPRINT",EDGE,{"derivedFrom":subQ1}),1.0]])]});}
            var Q7;
            {var subQ0=sQuery(id+"F11.wireOp",EDGE,"E221");Q7=makeQuery(id+"F11.imprint","IMPRINT",FACE,{"disambiguationData":[TD([[makeQuery(id+"F11.imprint","IMPRINT",EDGE,{"derivedFrom":subQ0}),-1.0]])]});}
            var Q8;
            {var subQ0=sQuery(id+"F11.wireOp",EDGE,"E228");Q8=makeQuery(id+"F11.imprint","IMPRINT",FACE,{"disambiguationData":[TD([[makeQuery(id+"F11.imprint","IMPRINT",EDGE,{"derivedFrom":subQ0}),-1.0]])]});}
            var Q9;
            {var subQ0=sQuery(id+"F11.wireOp",EDGE,"E237");Q9=makeQuery(id+"F11.imprint","IMPRINT",FACE,{"disambiguationData":[TD([[makeQuery(id+"F11.imprint","IMPRINT",EDGE,{"derivedFrom":subQ0}),-1.0]])]});}
            var Q10;
            {var subQ0=sQuery(id+"F11.wireOp",EDGE,"E246");Q10=makeQuery(id+"F11.imprint","IMPRINT",FACE,{"disambiguationData":[TD([[makeQuery(id+"F11.imprint","IMPRINT",EDGE,{"derivedFrom":subQ0}),-1.0]])]});}
            var Q11;
            {var subQ0=sQuery(id+"F11.wireOp",EDGE,"E251");Q11=makeQuery(id+"F11.imprint","IMPRINT",FACE,{"disambiguationData":[TD([[makeQuery(id+"F11.imprint","IMPRINT",EDGE,{"derivedFrom":subQ0}),-1.0]])]});}
            extrude(context, id + "F12", {"entities" : qUnion([Q0, Q1, Q2, Q3, Q4, Q5, Q6, Q7, Q8, Q9, Q10, Q11]), "depth" : 7.37 * mm});
        }
        {
            var Q0;
            {var subQ0=sQuery(id+"F11.wireOp",EDGE,"E193");var subQ8=makeQuery(id+"F11.imprint","INTERSECT",VERTEX,{"derivedFrom":[subQ0,sQuery(id+"F11.wireOp",EDGE,"E213"),sQuery(id+"F11.wireOp",EDGE,"E221")]});Q0=makeQuery(id+"F11.imprint","IMPRINT",FACE,{"disambiguationData":[TD([[makeQuery(id+"F11.imprint","IMPRINT",EDGE,{"disambiguationData":[TD([[subQ8,1.0]])],"derivedFrom":subQ0}),1.0]])]});}
            extrude(context, id + "F13", {"entities" : qUnion([Q0]), "depth" : 7.11 * mm});
        }
    });
